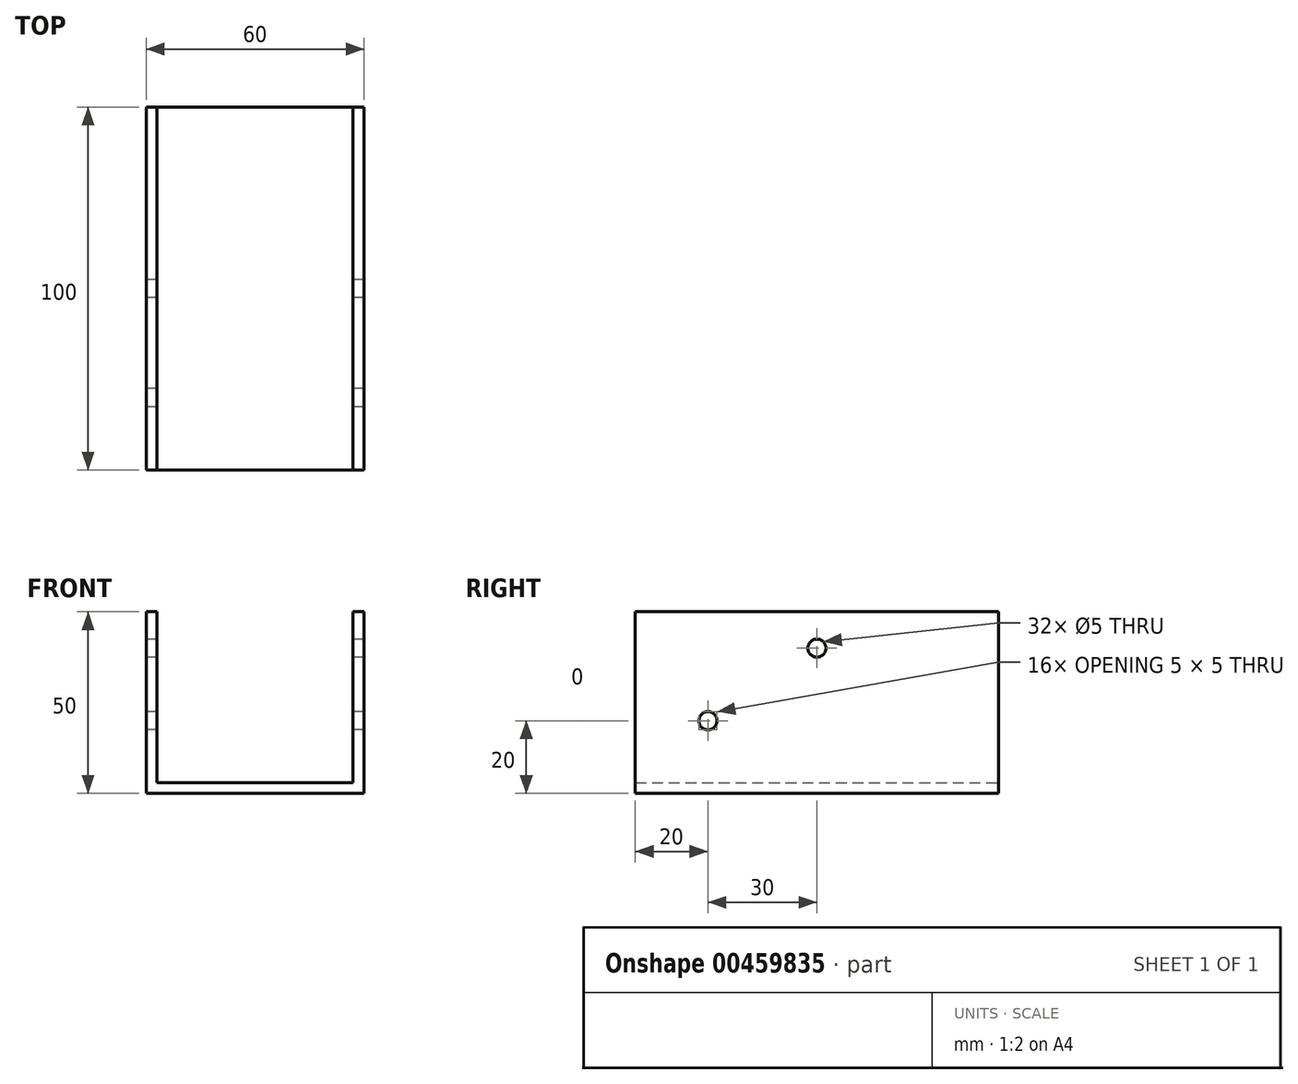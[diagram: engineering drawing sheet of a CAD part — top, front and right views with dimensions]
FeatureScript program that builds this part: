
annotation { "Feature Type Name" : "Feature", "Feature Type Description" : "" }
export const myFeature = defineFeature(function(context is Context, id is Id, definition is map)
    precondition{}
    {
        {
            var Q0;
            Q0=qCreatedBy(makeId("Front.planeOp"),FACE);
            var sketch = newSketch(context, id + "F0", { "sketchPlane" : qUnion([Q0])});
            skLineSegment(sketch, "E0", {"start": v(0, 0) * mm, "end": v(-30, 0) * mm});
            skLineSegment(sketch, "E1", {"start": v(-30, 0) * mm, "end": v(-30, 50) * mm});
            skLineSegment(sketch, "E2", {"start": v(-30, 50) * mm, "end": v(-27, 50) * mm});
            skLineSegment(sketch, "E3", {"start": v(-27, 50) * mm, "end": v(-27, 3) * mm});
            skLineSegment(sketch, "E4", {"start": v(-27, 3) * mm, "end": v(0, 3) * mm});
            skLineSegment(sketch, "E5", {"start": v(0, 3) * mm, "end": v(0, 0) * mm});
            skLineSegment(sketch, "E6.MirrorCS", {"start": v(30, 50) * mm, "end": v(27, 50) * mm});
            skLineSegment(sketch, "E7.MirrorCS", {"start": v(30, 0) * mm, "end": v(30, 50) * mm});
            skLineSegment(sketch, "E8.MirrorCS", {"start": v(27, 50) * mm, "end": v(27, 3) * mm});
            skLineSegment(sketch, "E9.MirrorCS", {"start": v(0, 0) * mm, "end": v(30, 0) * mm});
            skLineSegment(sketch, "E10.MirrorCS", {"start": v(27, 3) * mm, "end": v(0, 3) * mm});
            skSolve(sketch);
        }
        {
            var Q0;
            Q0 = qSketchRegion(id + "F0", true);
            extrude(context, id + "F1", {"entities" : qUnion([Q0]), "depth" : 100 * mm, "offsetDistance" : 25 * mm});
        }
        {
            var Q0;
            Q0=makeQuery(id+"F1.opExtrude","SWEPT_FACE",FACE,{"disambiguationData":[OSD([sQuery(id+"F0.wireOp",EDGE,"E1")])]});
            var sketch = newSketch(context, id + "F2", { "sketchPlane" : qUnion([Q0])});
            skCircle(sketch, "E11", {"center": v(80, 20) * mm, "radius": 2.5 * mm});
            skCircle(sketch, "E12", {"center": v(50, 40) * mm, "radius": 2.5 * mm});
            skSolve(sketch);
        }
        {
            var Q0;
            Q0 = qSketchRegion(id + "F2", true);
            extrude(context, id + "F3", {"entities" : qUnion([Q0]), "operationType" : NewBodyOperationType.REMOVE, "endBound" : BoundingType.THROUGH_ALL, "oppositeDirection" : true, "depth" : 25 * mm, "offsetDistance" : 25 * mm});
        }
    });
